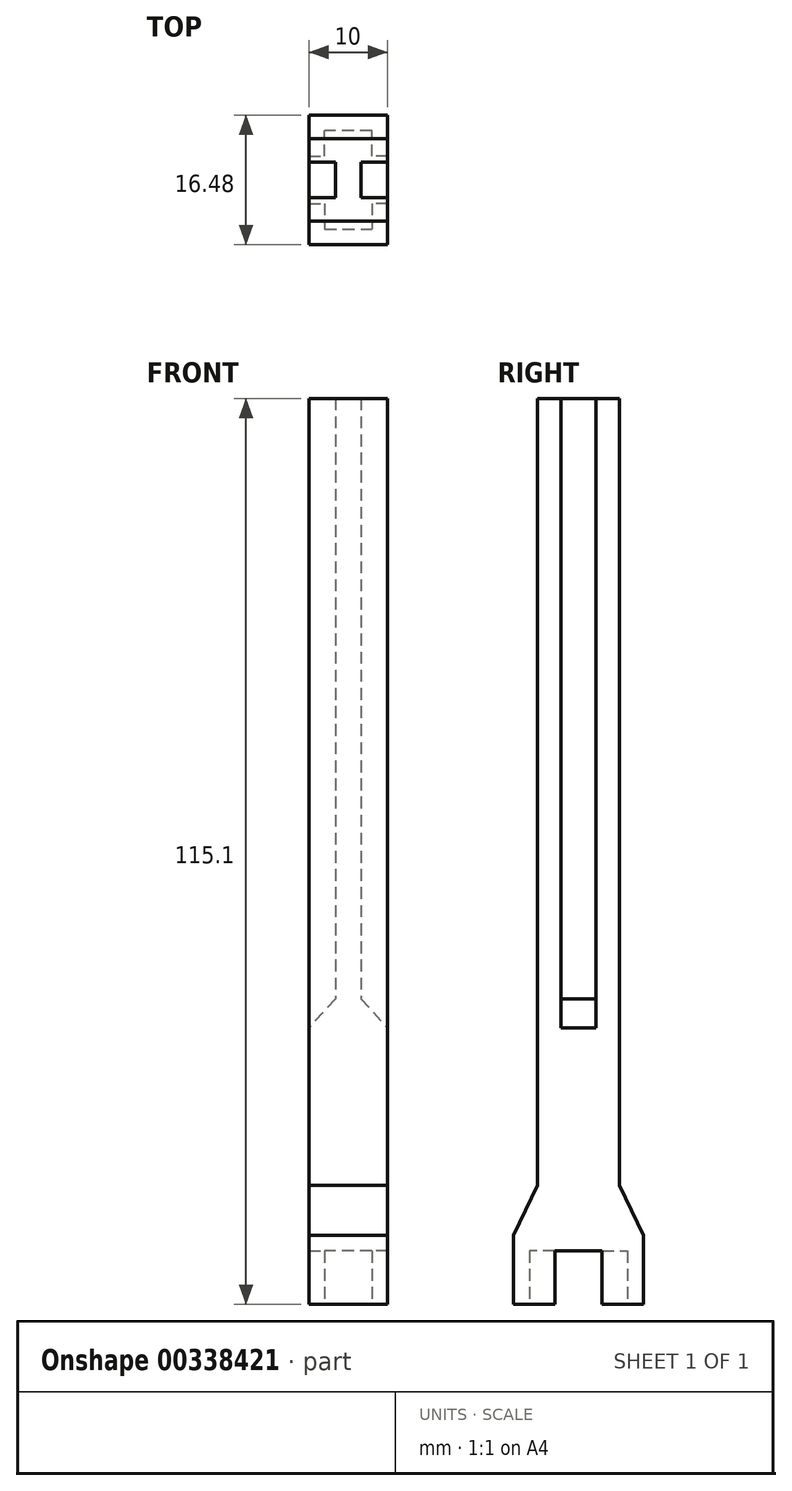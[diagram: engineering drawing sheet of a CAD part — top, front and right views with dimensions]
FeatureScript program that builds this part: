
annotation { "Feature Type Name" : "Feature", "Feature Type Description" : "" }
export const myFeature = defineFeature(function(context is Context, id is Id, definition is map)
    precondition{}
    {
        {
            var Q0;
            Q0=qCreatedBy(makeId("Top.planeOp"),FACE);
            var sketch = newSketch(context, id + "F0", { "sketchPlane" : qUnion([Q0])});
            skLineSegment(sketch, "E0.bottom", {"start": v(-5, 0) * mm, "end": v(-3, 0) * mm});
            skLineSegment(sketch, "E0.top", {"start": v(-5, 5.24) * mm, "end": v(0, 5.24) * mm});
            skLineSegment(sketch, "E0.left", {"start": v(-5, 0) * mm, "end": v(-5, 5.24) * mm});
            skLineSegment(sketch, "E1.top", {"start": v(0, 3.24) * mm, "end": v(-3, 3.24) * mm});
            skLineSegment(sketch, "E1.right", {"start": v(-3, 0) * mm, "end": v(-3, 3.24) * mm});
            skLineSegment(sketch, "E2.MirrorCS", {"start": v(5, 0) * mm, "end": v(5, 5.24) * mm});
            skLineSegment(sketch, "E3.MirrorCS", {"start": v(5, 5.24) * mm, "end": v(0, 5.24) * mm});
            skLineSegment(sketch, "E4.MirrorCS", {"start": v(0, 3.24) * mm, "end": v(3, 3.24) * mm});
            skLineSegment(sketch, "E5.MirrorCS", {"start": v(3, 0) * mm, "end": v(3, 3.24) * mm});
            skLineSegment(sketch, "E6.MirrorCS", {"start": v(5, 0) * mm, "end": v(3, 0) * mm});
            skLineSegment(sketch, "E7", {"start": v(-14.2, -3) * mm, "end": v(13.93, -3) * mm, "construction": true});
            skLineSegment(sketch, "E8.MirrorCS", {"start": v(-5, -6) * mm, "end": v(-3, -6) * mm});
            skLineSegment(sketch, "E9.MirrorCS", {"start": v(-5, -6) * mm, "end": v(-5, -11.24) * mm});
            skLineSegment(sketch, "E10.MirrorCS", {"start": v(-5, -11.24) * mm, "end": v(0, -11.24) * mm});
            skLineSegment(sketch, "E11.MirrorCS", {"start": v(5, -11.24) * mm, "end": v(0, -11.24) * mm});
            skLineSegment(sketch, "E12.MirrorCS", {"start": v(5, -6) * mm, "end": v(5, -11.24) * mm});
            skLineSegment(sketch, "E13.MirrorCS", {"start": v(5, -6) * mm, "end": v(3, -6) * mm});
            skLineSegment(sketch, "E14.MirrorCS", {"start": v(3, -6) * mm, "end": v(3, -9.24) * mm});
            skLineSegment(sketch, "E15.MirrorCS", {"start": v(0, -9.24) * mm, "end": v(3, -9.24) * mm});
            skLineSegment(sketch, "E16.MirrorCS", {"start": v(0, -9.24) * mm, "end": v(-3, -9.24) * mm});
            skLineSegment(sketch, "E17.MirrorCS", {"start": v(-3, -6) * mm, "end": v(-3, -9.24) * mm});
            skSolve(sketch);
        }
        {
            var Q0;
            Q0=qSketchRegion(id+"F0",true);
            extrude(context, id + "F1", {"entities" : qUnion([Q0]), "depth" : 6.8 * mm});
        }
        {
            var Q0;
            Q0=makeQuery(id+"F1.opExtrude","CAP_FACE",FACE,{"disambiguationData":[OSD([sQuery(id+"F0.wireOp",EDGE,"E0.bottom"),sQuery(id+"F0.wireOp",EDGE,"E0.top"),sQuery(id+"F0.wireOp",EDGE,"E0.left"),sQuery(id+"F0.wireOp",EDGE,"E1.top"),sQuery(id+"F0.wireOp",EDGE,"E1.right"),sQuery(id+"F0.wireOp",EDGE,"E2.MirrorCS"),sQuery(id+"F0.wireOp",EDGE,"E3.MirrorCS"),sQuery(id+"F0.wireOp",EDGE,"E4.MirrorCS"),sQuery(id+"F0.wireOp",EDGE,"E5.MirrorCS"),sQuery(id+"F0.wireOp",EDGE,"E6.MirrorCS")])],"isStart":false});
            var sketch = newSketch(context, id + "F2", { "sketchPlane" : qUnion([Q0])});
            skLineSegment(sketch, "E18.bottom", {"start": v(-5, 5.24) * mm, "end": v(5, 5.24) * mm});
            skLineSegment(sketch, "E18.top", {"start": v(-5, -11.24) * mm, "end": v(5, -11.24) * mm});
            skLineSegment(sketch, "E18.left", {"start": v(-5, 5.24) * mm, "end": v(-5, -11.24) * mm});
            skLineSegment(sketch, "E18.right", {"start": v(5, 5.24) * mm, "end": v(5, -11.24) * mm});
            skSolve(sketch);
        }
        {
            var Q0;
            {var subQ2=sQuery(id+"F2.wireOp",EDGE,"E18.top");Q0=makeQuery(id+"F2.imprint","IMPRINT",FACE,{"disambiguationData":[TD([[makeQuery(id+"F2.imprint","IMPRINT",EDGE,{"derivedFrom":subQ2}),1.0]])]});}
            var Q1;
            {var subQ3=sQuery(id+"F2.wireOp",EDGE,"E18.bottom");Q1=makeQuery(id+"F2.imprint","IMPRINT",FACE,{"disambiguationData":[TD([[makeQuery(id+"F2.imprint","IMPRINT",EDGE,{"derivedFrom":subQ3}),1.0]])]});}
            extrude(context, id + "F3", {"entities" : qUnion([Q0, Q1]), "depth" : 2 * mm});
        }
        {
            var Q0;
            Q0=makeQuery(id+"F1.opExtrude","SWEPT_BODY",BODY,{"disambiguationData":[OSD([sQuery(id+"F0.wireOp",EDGE,"E0.bottom"),sQuery(id+"F0.wireOp",EDGE,"E0.top"),sQuery(id+"F0.wireOp",EDGE,"E0.left"),sQuery(id+"F0.wireOp",EDGE,"E1.top"),sQuery(id+"F0.wireOp",EDGE,"E1.right"),sQuery(id+"F0.wireOp",EDGE,"E2.MirrorCS"),sQuery(id+"F0.wireOp",EDGE,"E3.MirrorCS"),sQuery(id+"F0.wireOp",EDGE,"E4.MirrorCS"),sQuery(id+"F0.wireOp",EDGE,"E5.MirrorCS"),sQuery(id+"F0.wireOp",EDGE,"E6.MirrorCS")])]});
            var Q1;
            Q1=makeQuery(id+"F1.opExtrude","SWEPT_BODY",BODY,{"disambiguationData":[OSD([sQuery(id+"F0.wireOp",EDGE,"E8.MirrorCS"),sQuery(id+"F0.wireOp",EDGE,"E9.MirrorCS"),sQuery(id+"F0.wireOp",EDGE,"E10.MirrorCS"),sQuery(id+"F0.wireOp",EDGE,"E11.MirrorCS"),sQuery(id+"F0.wireOp",EDGE,"E12.MirrorCS"),sQuery(id+"F0.wireOp",EDGE,"E13.MirrorCS"),sQuery(id+"F0.wireOp",EDGE,"E14.MirrorCS"),sQuery(id+"F0.wireOp",EDGE,"E15.MirrorCS"),sQuery(id+"F0.wireOp",EDGE,"E16.MirrorCS"),sQuery(id+"F0.wireOp",EDGE,"E17.MirrorCS")])]});
            var Q2;
            Q2=makeQuery(id+"F3.opExtrude","SWEPT_BODY",BODY,{"disambiguationData":[OSD([sQuery(id+"F2.wireOp",EDGE,"E18.bottom"),sQuery(id+"F2.wireOp",EDGE,"E18.top"),sQuery(id+"F2.wireOp",EDGE,"E18.left"),sQuery(id+"F2.wireOp",EDGE,"E18.right")])]});
            booleanBodies(context, id + "F4", {"operationType" : BooleanOperationType.UNION, "tools" : qUnion([Q0, Q1, Q2])});
        }
        {
            var Q0;
            Q0=makeQuery(id+"F3.opExtrude","CAP_FACE",FACE,{"disambiguationData":[OSD([sQuery(id+"F2.wireOp",EDGE,"E18.bottom"),sQuery(id+"F2.wireOp",EDGE,"E18.top"),sQuery(id+"F2.wireOp",EDGE,"E18.left"),sQuery(id+"F2.wireOp",EDGE,"E18.right")])],"isStart":false});
            cPlane(context, id + "F5", {"entities" : qUnion([Q0]), "cplaneType" : CPlaneType.OFFSET, "offset" : 6.3 * mm, "width" : 150 * mm, "height" : 150 * mm});
        }
        {
            var Q0;
            Q0=qCreatedBy(id+"F5.planeOp",FACE);
            var sketch = newSketch(context, id + "F6", { "sketchPlane" : qUnion([Q0])});
            skLineSegment(sketch, "E19.bottom", {"start": v(-5, 2.24) * mm, "end": v(5, 2.24) * mm});
            skLineSegment(sketch, "E19.top", {"start": v(-5, -8.24) * mm, "end": v(5, -8.24) * mm});
            skLineSegment(sketch, "E19.left", {"start": v(-5, 2.24) * mm, "end": v(-5, -8.24) * mm});
            skLineSegment(sketch, "E19.right", {"start": v(5, 2.24) * mm, "end": v(5, -8.24) * mm});
            skSolve(sketch);
        }
        {
            var Q1;
            Q1=makeQuery(id+"F3.opExtrude","CAP_FACE",FACE,{"disambiguationData":[OSD([sQuery(id+"F2.wireOp",EDGE,"E18.bottom"),sQuery(id+"F2.wireOp",EDGE,"E18.top"),sQuery(id+"F2.wireOp",EDGE,"E18.left"),sQuery(id+"F2.wireOp",EDGE,"E18.right")])],"isStart":false});
            var Q2;
            Q2=makeQuery(id+"F6.imprint","IMPRINT",FACE,{"disambiguationData":[TD([[makeQuery(id+"F6.imprint","IMPRINT",EDGE,{"derivedFrom":sQuery(id+"F6.wireOp",EDGE,"E19.bottom")}),-1.0]])]});
            loft(context, id + "F7", {"operationType" : NewBodyOperationType.ADD, "sheetProfilesArray" : [{ "sheetProfileEntities" : qUnion([Q1]) }, { "sheetProfileEntities" : qUnion([Q2]) }]});
        }
        {
            var Q0;
            Q0=makeQuery(id+"F7.opLoft","CAP_FACE",FACE,{"disambiguationData":[OSD([makeQuery(id+"F6.imprint","IMPRINT",FACE,{"disambiguationData":[TD([[makeQuery(id+"F6.imprint","IMPRINT",EDGE,{"derivedFrom":sQuery(id+"F6.wireOp",EDGE,"E19.bottom")}),-1.0]])]})])],"isStart":true});
            var sketch = newSketch(context, id + "F8", { "sketchPlane" : qUnion([Q0])});
            skLineSegment(sketch, "E20.bottom", {"start": v(-5, 2.24) * mm, "end": v(5, 2.24) * mm});
            skLineSegment(sketch, "E20.top", {"start": v(-5, -8.24) * mm, "end": v(5, -8.24) * mm});
            skLineSegment(sketch, "E20.left", {"start": v(-5, 2.24) * mm, "end": v(-5, -8.24) * mm});
            skLineSegment(sketch, "E20.right", {"start": v(5, 2.24) * mm, "end": v(5, -8.24) * mm});
            skLineSegment(sketch, "E21.bottom", {"start": v(-5, -0.76) * mm, "end": v(-1.65, -0.76) * mm});
            skLineSegment(sketch, "E21.top", {"start": v(-5, -5.24) * mm, "end": v(-1.65, -5.24) * mm});
            skLineSegment(sketch, "E21.left", {"start": v(-5, -0.76) * mm, "end": v(-5, -5.24) * mm});
            skLineSegment(sketch, "E21.right", {"start": v(-1.65, -0.76) * mm, "end": v(-1.65, -5.24) * mm});
            skLineSegment(sketch, "E22", {"start": v(0, 2.24) * mm, "end": v(0, -8.24) * mm, "construction": true});
            skLineSegment(sketch, "E23.MirrorCS", {"start": v(1.65, -0.76) * mm, "end": v(1.65, -5.24) * mm});
            skLineSegment(sketch, "E24.MirrorCS", {"start": v(5, -0.76) * mm, "end": v(1.65, -0.76) * mm});
            skLineSegment(sketch, "E25.MirrorCS", {"start": v(5, -5.24) * mm, "end": v(1.65, -5.24) * mm});
            skSolve(sketch);
        }
        {
            var Q0;
            {var subQ4=sQuery(id+"F8.wireOp",EDGE,"E20.bottom");Q0=makeQuery(id+"F8.imprint","IMPRINT",FACE,{"disambiguationData":[TD([[makeQuery(id+"F8.imprint","IMPRINT",EDGE,{"derivedFrom":subQ4}),1.0]])]});}
            extrude(context, id + "F9", {"entities" : qUnion([Q0]), "operationType" : NewBodyOperationType.ADD, "depth" : 100 * mm});
        }
        {
            var Q0;
            {var subQ4=sQuery(id+"F6.wireOp",EDGE,"E19.bottom");Q0=makeQuery(id+"F9.boolean.opBoolean","SPLIT",FACE,{"disambiguationData":[TD([makeQuery(id+"F1.opExtrude","SWEPT_FACE",FACE,{"disambiguationData":[OSD([sQuery(id+"F0.wireOp",EDGE,"E2.MirrorCS")])]})])],"derivedFrom":makeQuery(id+"F7.opLoft","CAP_FACE",FACE,{"disambiguationData":[OSD([makeQuery(id+"F6.imprint","IMPRINT",FACE,{"disambiguationData":[TD([[makeQuery(id+"F6.imprint","IMPRINT",EDGE,{"derivedFrom":subQ4}),-1.0]])]})])],"isStart":true})});}
            var sketch = newSketch(context, id + "F10", { "sketchPlane" : qUnion([Q0])});
            skLineSegment(sketch, "E26.bottom", {"start": v(1.65, -0.76) * mm, "end": v(5, -0.76) * mm});
            skLineSegment(sketch, "E26.top", {"start": v(1.65, -5.24) * mm, "end": v(5, -5.24) * mm});
            skLineSegment(sketch, "E26.left", {"start": v(1.65, -0.76) * mm, "end": v(1.65, -5.24) * mm});
            skLineSegment(sketch, "E26.right", {"start": v(5, -0.76) * mm, "end": v(5, -5.24) * mm});
            skSolve(sketch);
        }
        {
            var Q0;
            Q0=makeQuery(id+"F10.imprint","IMPRINT",FACE,{"disambiguationData":[TD([[makeQuery(id+"F10.imprint","IMPRINT",EDGE,{"derivedFrom":sQuery(id+"F10.wireOp",EDGE,"E26.bottom")}),1.0]])]});
            extrude(context, id + "F11", {"entities" : qUnion([Q0]), "operationType" : NewBodyOperationType.ADD, "depth" : 20 * mm});
        }
        {
            var Q0;
            Q0=makeQuery(id+"F9.opExtrude","SWEPT_FACE",FACE,{"disambiguationData":[OSD([sQuery(id+"F8.wireOp",EDGE,"E24.MirrorCS")])]});
            var sketch = newSketch(context, id + "F12", { "sketchPlane" : qUnion([Q0])});
            skLineSegment(sketch, "E27", {"start": v(5, 35.1) * mm, "end": v(1.65, 38.82) * mm});
            skSolve(sketch);
        }
        {
            var Q0;
            {var subQ0=sQuery(id+"F12.wireOp",EDGE,"E27");Q0=makeQuery(id+"F12.imprint","IMPRINT",FACE,{"disambiguationData":[TD([[makeQuery(id+"F12.imprint","IMPRINT",EDGE,{"derivedFrom":subQ0}),1.0]])]});}
            extrude(context, id + "F13", {"entities" : qUnion([Q0]), "operationType" : NewBodyOperationType.ADD, "depth" : 4.8 * mm});
        }
        {
            var Q0;
            Q0=makeQuery(id+"F1.opExtrude","SWEPT_BODY",BODY,{"disambiguationData":[OSD([sQuery(id+"F0.wireOp",EDGE,"E0.bottom"),sQuery(id+"F0.wireOp",EDGE,"E0.top"),sQuery(id+"F0.wireOp",EDGE,"E0.left"),sQuery(id+"F0.wireOp",EDGE,"E1.top"),sQuery(id+"F0.wireOp",EDGE,"E1.right"),sQuery(id+"F0.wireOp",EDGE,"E2.MirrorCS"),sQuery(id+"F0.wireOp",EDGE,"E3.MirrorCS"),sQuery(id+"F0.wireOp",EDGE,"E4.MirrorCS"),sQuery(id+"F0.wireOp",EDGE,"E5.MirrorCS"),sQuery(id+"F0.wireOp",EDGE,"E6.MirrorCS")])]});
            var Q1;
            Q1=qCreatedBy(makeId("Right.planeOp"),FACE);
            mirror(context, id + "F14", {"operationType" : NewBodyOperationType.ADD, "entities" : qUnion([Q0]), "mirrorPlane" : qUnion([Q1])});
        }
    });
